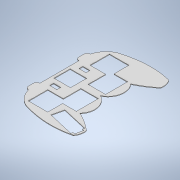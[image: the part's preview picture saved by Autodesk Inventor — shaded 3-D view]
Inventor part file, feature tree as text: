
AUTODESK INVENTOR PART (.ipt)
format: ipt  version: 2022 (Build 260153000, 153)  size: 312,320 bytes
history: native  units: mm
features: sketch x2, extrude x1
ambient origin geometry x8: Origin, YZ Plane, XZ Plane, XY Plane, X Axis, Y Axis, Z Axis, Center Point
bodies: Solid1 (feature_tree)
feature tree (3):
  sketch  "Sketch1"  dims[d0=35.0mm d1=60.0mm]
  extrude  "Extrusion1"  Depth=60.0mm
  sketch  "Sketch2"  dims[d2=17.5mm d3=25.0mm d4=22.5mm d6=25.0mm d7=27.0mm d8=34.0mm d9=27.0mm d10=7.5mm d11=25.0mm d12=27.0mm d13=34.0mm d14=27.0mm d15=6.0mm d16=6.0mm d17=6.0mm d18=6.5mm d22=6.0mm d23=40.0mm d25=360.0deg d27=25.0mm d28=27.0mm d31=40.0mm d32=25.0mm d33=27.0mm d34=5.0mm d35=8.0mm d36=8.0mm d37=35.0mm d38=8.0mm d39=12.0mm d40=8.0mm d41=60.0mm d42=17.5mm d47=4.0mm d48=7.5mm d49=22.5mm d50=25.0mm d51=27.0mm d52=34.0mm d53=6.5mm d54=3.0mm d55=3.0mm d56=6.0mm d57=6.0mm d58=40.0mm d60=360.0deg d62=50.0mm d63=1.0mm d64=0.0mm d65=1.5mm d66=12.5mm d67=27.0mm d68=25.0mm d69=1.401mm d70=13.425896mm d71=200.0mm d72=37.3mm d73=4.0mm d74=37.3mm d75=15.0mm d76=15.0mm d77=30.0mm d78=30.0mm d79=48.0mm d80=9.0mm d81=9.0mm d82=3.0mm d83=3.0mm d84=3.0mm d85=3.0mm d86=6.5mm d87=14.0mm d88=3.0mm d89=1.5mm d90=1.5mm d91=3.0mm]
